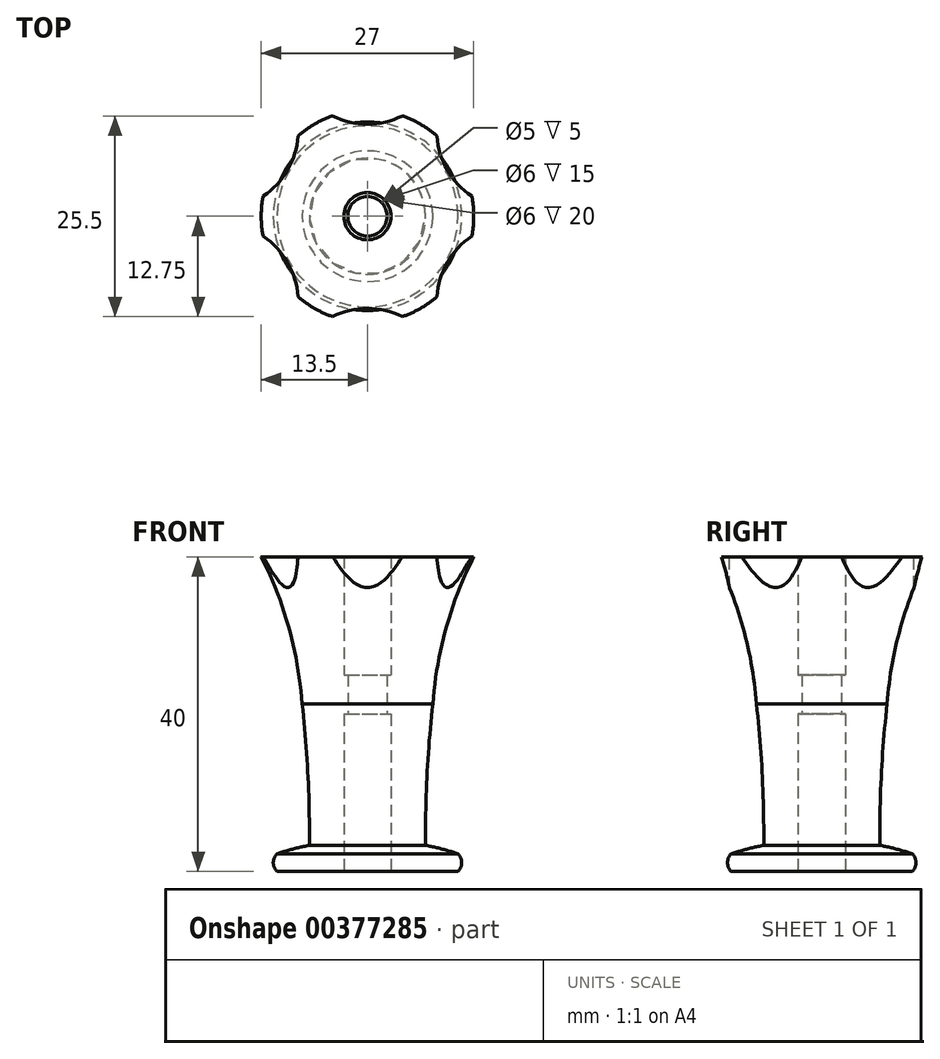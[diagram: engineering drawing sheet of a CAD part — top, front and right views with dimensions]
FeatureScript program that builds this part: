
annotation { "Feature Type Name" : "Feature", "Feature Type Description" : "" }
export const myFeature = defineFeature(function(context is Context, id is Id, definition is map)
    precondition{}
    {
        {
            var Q0;
            Q0=qCreatedBy(makeId("Front.planeOp"),FACE);
            var sketch = newSketch(context, id + "F0", { "sketchPlane" : qUnion([Q0])});
            skLineSegment(sketch, "E0", {"start": v(0, 19.97) * mm, "end": v(0, -20.03) * mm});
            skLineSegment(sketch, "E1", {"start": v(0, 19.97) * mm, "end": v(13.5, 19.97) * mm});
            skLineSegment(sketch, "E2", {"start": v(0, -20.03) * mm, "end": v(11.5, -20.03) * mm});
            skArc(sketch, "E3", {"start": v(11.5, -20.03) * mm, "mid": v(11.97, -18.9) * mm, "end": v(11.5, -17.77) * mm});
            skArc(sketch, "E4", {"start": v(11.5, -17.77) * mm, "mid": v(9.46, -17.16) * mm, "end": v(7.37, -16.69) * mm});
            skArc(sketch, "E5", {"start": v(13.5, 19.97) * mm, "mid": v(9.97, 10.87) * mm, "end": v(8.3, 1.26) * mm});
            skArc(sketch, "E6", {"start": v(8.3, 1.26) * mm, "mid": v(7.57, -7.7) * mm, "end": v(7.37, -16.69) * mm});
            skSolve(sketch);
        }
        {
            var Q0;
            Q0 = qSketchRegion(id + "F0", true);
            var Q1;
            Q1=sQuery(id+"F0.wireOp",EDGE,"E0");
            revolve(context, id + "F1", {"entities" : qUnion([Q0]), "axis" : qUnion([Q1]), "revolveType" : RevolveType.FULL});
        }
        {
            var Q0;
            Q0=makeQuery(id+"F1.opRevolve","SWEPT_FACE",FACE,{"disambiguationData":[OSD([sQuery(id+"F0.wireOp",EDGE,"E1")])]});
            var sketch = newSketch(context, id + "F2", { "sketchPlane" : qUnion([Q0])});
            skCircle(sketch, "E7.cCircle", {"center": v(0, 0) * mm, "radius": 13.5 * mm, "construction": true});
            skLineSegment(sketch, "E7.0", {"start": v(-13.5, -7.8) * mm, "end": v(-13.5, 7.8) * mm});
            skLineSegment(sketch, "E7.1", {"start": v(-13.5, 7.8) * mm, "end": v(0, 15.59) * mm});
            skLineSegment(sketch, "E7.2", {"start": v(0, 15.59) * mm, "end": v(13.5, 7.8) * mm});
            skLineSegment(sketch, "E7.3", {"start": v(13.5, 7.8) * mm, "end": v(13.5, -7.8) * mm});
            skLineSegment(sketch, "E7.4", {"start": v(13.5, -7.8) * mm, "end": v(0, -15.59) * mm});
            skLineSegment(sketch, "E7.5", {"start": v(0, -15.59) * mm, "end": v(-13.5, -7.8) * mm});
            skPoint(sketch, "E7.0.midPoint", {"position": v(-13.5, 0) * mm});
            skLineSegment(sketch, "E8.0", {"start": v(-13.5, -4.91) * mm, "end": v(-13.5, 4.91) * mm});
            skLineSegment(sketch, "E8.1", {"start": v(-13.5, 4.91) * mm, "end": v(-7.18, 12.44) * mm});
            skLineSegment(sketch, "E8.2", {"start": v(-7.18, 12.44) * mm, "end": v(2.5, 14.15) * mm});
            skLineSegment(sketch, "E8.3", {"start": v(2.5, 14.15) * mm, "end": v(11, 9.23) * mm});
            skLineSegment(sketch, "E8.4", {"start": v(11, 9.23) * mm, "end": v(14.37, 0) * mm});
            skLineSegment(sketch, "E8.5", {"start": v(14.37, 0) * mm, "end": v(11, -9.23) * mm});
            skLineSegment(sketch, "E8.6", {"start": v(11, -9.23) * mm, "end": v(2.5, -14.15) * mm});
            skLineSegment(sketch, "E8.7", {"start": v(2.5, -14.15) * mm, "end": v(-7.18, -12.44) * mm});
            skLineSegment(sketch, "E8.8", {"start": v(-7.18, -12.44) * mm, "end": v(-13.5, -4.91) * mm});
            skLineSegment(sketch, "E9.0", {"start": v(13.5, 4.91) * mm, "end": v(13.5, -4.91) * mm});
            skLineSegment(sketch, "E9.1", {"start": v(13.5, -4.91) * mm, "end": v(7.18, -12.44) * mm});
            skLineSegment(sketch, "E9.2", {"start": v(7.18, -12.44) * mm, "end": v(-2.5, -14.15) * mm});
            skLineSegment(sketch, "E9.3", {"start": v(-2.5, -14.15) * mm, "end": v(-11, -9.23) * mm});
            skLineSegment(sketch, "E9.4", {"start": v(-11, -9.23) * mm, "end": v(-14.37, 0) * mm});
            skLineSegment(sketch, "E9.5", {"start": v(-14.37, 0) * mm, "end": v(-11, 9.23) * mm});
            skLineSegment(sketch, "E9.6", {"start": v(-11, 9.23) * mm, "end": v(-2.5, 14.15) * mm});
            skLineSegment(sketch, "E9.7", {"start": v(-2.5, 14.15) * mm, "end": v(7.18, 12.44) * mm});
            skLineSegment(sketch, "E9.8", {"start": v(7.18, 12.44) * mm, "end": v(13.5, 4.91) * mm});
            skPoint(sketch, "E9.0.midPoint", {"position": v(13.5, 0) * mm});
            skArc(sketch, "E10", {"start": v(-4.69, 12.88) * mm, "mid": v(0, 11.71) * mm, "end": v(4.69, 12.88) * mm});
            skArc(sketch, "E11", {"start": v(4.69, -12.88) * mm, "mid": v(0, -11.71) * mm, "end": v(-4.69, -12.88) * mm});
            skArc(sketch, "E12", {"start": v(-13.5, 2.38) * mm, "mid": v(-10.14, 5.86) * mm, "end": v(-8.81, 10.5) * mm});
            skArc(sketch, "E13", {"start": v(-8.81, -10.5) * mm, "mid": v(-10.14, -5.86) * mm, "end": v(-13.5, -2.38) * mm});
            skArc(sketch, "E14", {"start": v(13.5, -2.38) * mm, "mid": v(10.14, -5.86) * mm, "end": v(8.81, -10.5) * mm});
            skArc(sketch, "E15", {"start": v(8.81, 10.5) * mm, "mid": v(10.14, 5.86) * mm, "end": v(13.5, 2.38) * mm});
            skCircle(sketch, "E16", {"center": v(0, 0) * mm, "radius": 11.23 * mm});
            skSolve(sketch);
        }
        {
            var Q0;
            Q0=makeQuery(id+"F1.opRevolve","SWEPT_FACE",FACE,{"disambiguationData":[OSD([sQuery(id+"F0.wireOp",EDGE,"E2")])]});
            var sketch = newSketch(context, id + "F3", { "sketchPlane" : qUnion([Q0])});
            skCircle(sketch, "E17", {"center": v(0, 0) * mm, "radius": 3 * mm});
            skSolve(sketch);
        }
        {
            var Q0;
            Q0 = qSketchRegion(id + "F3", true);
            extrude(context, id + "F4", {"entities" : qUnion([Q0]), "operationType" : NewBodyOperationType.REMOVE, "oppositeDirection" : true, "depth" : 50 * mm});
        }
        {
            var Q0;
            {var subQ0=sQuery(id+"F2.wireOp",EDGE,"E7.5");var subQ1=sQuery(id+"F2.wireOp",EDGE,"E7.0");var subQ2=makeQuery(id+"F2.imprint","INTERSECT",VERTEX,{"derivedFrom":[subQ1,subQ0]});Q0=makeQuery(id+"F2.imprint","IMPRINT",FACE,{"disambiguationData":[TD([[makeQuery(id+"F2.imprint","IMPRINT",EDGE,{"disambiguationData":[TD([[subQ2,-1.0]])],"derivedFrom":subQ1}),-1.0]])]});}
            var Q1;
            {var subQ0=sQuery(id+"F2.wireOp",EDGE,"E7.1");var subQ1=sQuery(id+"F2.wireOp",EDGE,"E7.0");var subQ2=makeQuery(id+"F2.imprint","INTERSECT",VERTEX,{"derivedFrom":[subQ1,subQ0]});Q1=makeQuery(id+"F2.imprint","IMPRINT",FACE,{"disambiguationData":[TD([[makeQuery(id+"F2.imprint","IMPRINT",EDGE,{"disambiguationData":[TD([[subQ2,1.0]])],"derivedFrom":subQ1}),-1.0]])]});}
            var Q2;
            {var subQ0=sQuery(id+"F2.wireOp",EDGE,"E7.2");var subQ1=sQuery(id+"F2.wireOp",EDGE,"E7.1");var subQ2=makeQuery(id+"F2.imprint","INTERSECT",VERTEX,{"derivedFrom":[subQ1,subQ0]});Q2=makeQuery(id+"F2.imprint","IMPRINT",FACE,{"disambiguationData":[TD([[makeQuery(id+"F2.imprint","IMPRINT",EDGE,{"disambiguationData":[TD([[subQ2,1.0]])],"derivedFrom":subQ1}),-1.0]])]});}
            var Q3;
            {var subQ0=sQuery(id+"F2.wireOp",EDGE,"E7.3");var subQ1=sQuery(id+"F2.wireOp",EDGE,"E7.2");var subQ2=makeQuery(id+"F2.imprint","INTERSECT",VERTEX,{"derivedFrom":[subQ1,subQ0]});Q3=makeQuery(id+"F2.imprint","IMPRINT",FACE,{"disambiguationData":[TD([[makeQuery(id+"F2.imprint","IMPRINT",EDGE,{"disambiguationData":[TD([[subQ2,1.0]])],"derivedFrom":subQ1}),-1.0]])]});}
            var Q4;
            {var subQ0=sQuery(id+"F2.wireOp",EDGE,"E7.4");var subQ1=sQuery(id+"F2.wireOp",EDGE,"E7.3");var subQ2=makeQuery(id+"F2.imprint","INTERSECT",VERTEX,{"derivedFrom":[subQ1,subQ0]});Q4=makeQuery(id+"F2.imprint","IMPRINT",FACE,{"disambiguationData":[TD([[makeQuery(id+"F2.imprint","IMPRINT",EDGE,{"disambiguationData":[TD([[subQ2,1.0]])],"derivedFrom":subQ1}),-1.0]])]});}
            var Q5;
            {var subQ0=sQuery(id+"F2.wireOp",EDGE,"E7.5");var subQ1=sQuery(id+"F2.wireOp",EDGE,"E7.4");var subQ2=makeQuery(id+"F2.imprint","INTERSECT",VERTEX,{"derivedFrom":[subQ1,subQ0]});Q5=makeQuery(id+"F2.imprint","IMPRINT",FACE,{"disambiguationData":[TD([[makeQuery(id+"F2.imprint","IMPRINT",EDGE,{"disambiguationData":[TD([[subQ2,1.0]])],"derivedFrom":subQ1}),-1.0]])]});}
            var Q6;
            {var subQ0=sQuery(id+"F2.wireOp",EDGE,"E9.4");var subQ4=sQuery(id+"F2.wireOp",EDGE,"E9.5");var subQ5=makeQuery(id+"F2.imprint","INTERSECT",VERTEX,{"derivedFrom":[subQ0,subQ4]});Q6=makeQuery(id+"F2.imprint","IMPRINT",FACE,{"disambiguationData":[TD([[makeQuery(id+"F2.imprint","IMPRINT",EDGE,{"disambiguationData":[TD([[subQ5,1.0]])],"derivedFrom":subQ0}),-1.0]])]});}
            var Q7;
            {var subQ0=sQuery(id+"F2.wireOp",EDGE,"E8.2");var subQ1=sQuery(id+"F2.wireOp",EDGE,"E8.1");var subQ2=makeQuery(id+"F2.imprint","INTERSECT",VERTEX,{"derivedFrom":[subQ1,subQ0]});Q7=makeQuery(id+"F2.imprint","IMPRINT",FACE,{"disambiguationData":[TD([[makeQuery(id+"F2.imprint","IMPRINT",EDGE,{"disambiguationData":[TD([[subQ2,1.0]])],"derivedFrom":subQ1}),-1.0]])]});}
            var Q8;
            {var subQ0=sQuery(id+"F2.wireOp",EDGE,"E9.7");var subQ4=sQuery(id+"F2.wireOp",EDGE,"E9.8");var subQ5=makeQuery(id+"F2.imprint","INTERSECT",VERTEX,{"derivedFrom":[subQ0,subQ4]});Q8=makeQuery(id+"F2.imprint","IMPRINT",FACE,{"disambiguationData":[TD([[makeQuery(id+"F2.imprint","IMPRINT",EDGE,{"disambiguationData":[TD([[subQ5,1.0]])],"derivedFrom":subQ0}),-1.0]])]});}
            var Q9;
            {var subQ0=sQuery(id+"F2.wireOp",EDGE,"E8.5");var subQ1=sQuery(id+"F2.wireOp",EDGE,"E8.4");var subQ2=makeQuery(id+"F2.imprint","INTERSECT",VERTEX,{"derivedFrom":[subQ1,subQ0]});Q9=makeQuery(id+"F2.imprint","IMPRINT",FACE,{"disambiguationData":[TD([[makeQuery(id+"F2.imprint","IMPRINT",EDGE,{"disambiguationData":[TD([[subQ2,1.0]])],"derivedFrom":subQ1}),-1.0]])]});}
            var Q10;
            {var subQ0=sQuery(id+"F2.wireOp",EDGE,"E9.1");var subQ4=sQuery(id+"F2.wireOp",EDGE,"E9.2");var subQ6=makeQuery(id+"F2.imprint","INTERSECT",VERTEX,{"derivedFrom":[subQ0,subQ4]});Q10=makeQuery(id+"F2.imprint","IMPRINT",FACE,{"disambiguationData":[TD([[makeQuery(id+"F2.imprint","IMPRINT",EDGE,{"disambiguationData":[TD([[subQ6,1.0]])],"derivedFrom":subQ0}),-1.0]])]});}
            var Q11;
            {var subQ0=sQuery(id+"F2.wireOp",EDGE,"E8.8");var subQ1=sQuery(id+"F2.wireOp",EDGE,"E8.7");var subQ2=makeQuery(id+"F2.imprint","INTERSECT",VERTEX,{"derivedFrom":[subQ1,subQ0]});Q11=makeQuery(id+"F2.imprint","IMPRINT",FACE,{"disambiguationData":[TD([[makeQuery(id+"F2.imprint","IMPRINT",EDGE,{"disambiguationData":[TD([[subQ2,1.0]])],"derivedFrom":subQ1}),-1.0]])]});}
            var Q12;
            {var subQ0=sQuery(id+"F2.wireOp",EDGE,"E8.8");var subQ3=sQuery(id+"F2.wireOp",EDGE,"E9.4");var subQ5=makeQuery(id+"F2.imprint","INTERSECT",VERTEX,{"derivedFrom":[subQ0,subQ3]});Q12=makeQuery(id+"F2.imprint","IMPRINT",FACE,{"disambiguationData":[TD([[makeQuery(id+"F2.imprint","IMPRINT",EDGE,{"disambiguationData":[TD([[subQ5,-1.0]])],"derivedFrom":subQ0}),-1.0]])]});}
            var Q13;
            {var subQ0=sQuery(id+"F2.wireOp",EDGE,"E8.1");var subQ3=sQuery(id+"F2.wireOp",EDGE,"E9.5");var subQ5=makeQuery(id+"F2.imprint","INTERSECT",VERTEX,{"derivedFrom":[subQ0,subQ3]});Q13=makeQuery(id+"F2.imprint","IMPRINT",FACE,{"disambiguationData":[TD([[makeQuery(id+"F2.imprint","IMPRINT",EDGE,{"disambiguationData":[TD([[subQ5,1.0]])],"derivedFrom":subQ0}),-1.0]])]});}
            var Q14;
            {var subQ0=sQuery(id+"F2.wireOp",EDGE,"E9.5");var subQ1=sQuery(id+"F2.wireOp",EDGE,"E8.1");var subQ2=makeQuery(id+"F2.imprint","INTERSECT",VERTEX,{"derivedFrom":[subQ1,subQ0]});Q14=makeQuery(id+"F2.imprint","IMPRINT",FACE,{"disambiguationData":[TD([[makeQuery(id+"F2.imprint","IMPRINT",EDGE,{"disambiguationData":[TD([[subQ2,-1.0]])],"derivedFrom":subQ1}),1.0]])]});}
            var Q15;
            {var subQ1=sQuery(id+"F2.wireOp",EDGE,"E8.2");var subQ4=sQuery(id+"F2.wireOp",EDGE,"E9.7");var subQ6=makeQuery(id+"F2.imprint","INTERSECT",VERTEX,{"derivedFrom":[subQ1,subQ4]});Q15=makeQuery(id+"F2.imprint","IMPRINT",FACE,{"disambiguationData":[TD([[makeQuery(id+"F2.imprint","IMPRINT",EDGE,{"disambiguationData":[TD([[subQ6,1.0]])],"derivedFrom":subQ1}),1.0]])]});}
            var Q16;
            {var subQ1=sQuery(id+"F2.wireOp",EDGE,"E8.2");var subQ3=sQuery(id+"F2.wireOp",EDGE,"E9.7");var subQ4=makeQuery(id+"F2.imprint","INTERSECT",VERTEX,{"derivedFrom":[subQ1,subQ3]});Q16=makeQuery(id+"F2.imprint","IMPRINT",FACE,{"disambiguationData":[TD([[makeQuery(id+"F2.imprint","IMPRINT",EDGE,{"disambiguationData":[TD([[subQ4,-1.0]])],"derivedFrom":subQ1}),-1.0]])]});}
            var Q17;
            {var subQ0=sQuery(id+"F2.wireOp",EDGE,"E8.4");var subQ3=sQuery(id+"F2.wireOp",EDGE,"E9.8");var subQ5=makeQuery(id+"F2.imprint","INTERSECT",VERTEX,{"derivedFrom":[subQ0,subQ3]});Q17=makeQuery(id+"F2.imprint","IMPRINT",FACE,{"disambiguationData":[TD([[makeQuery(id+"F2.imprint","IMPRINT",EDGE,{"disambiguationData":[TD([[subQ5,1.0]])],"derivedFrom":subQ0}),-1.0]])]});}
            var Q18;
            {var subQ0=sQuery(id+"F2.wireOp",EDGE,"E9.8");var subQ1=sQuery(id+"F2.wireOp",EDGE,"E8.4");var subQ2=makeQuery(id+"F2.imprint","INTERSECT",VERTEX,{"derivedFrom":[subQ1,subQ0]});Q18=makeQuery(id+"F2.imprint","IMPRINT",FACE,{"disambiguationData":[TD([[makeQuery(id+"F2.imprint","IMPRINT",EDGE,{"disambiguationData":[TD([[subQ2,-1.0]])],"derivedFrom":subQ1}),1.0]])]});}
            var Q19;
            {var subQ1=sQuery(id+"F2.wireOp",EDGE,"E8.5");var subQ4=sQuery(id+"F2.wireOp",EDGE,"E9.1");var subQ5=makeQuery(id+"F2.imprint","INTERSECT",VERTEX,{"derivedFrom":[subQ1,subQ4]});Q19=makeQuery(id+"F2.imprint","IMPRINT",FACE,{"disambiguationData":[TD([[makeQuery(id+"F2.imprint","IMPRINT",EDGE,{"disambiguationData":[TD([[subQ5,1.0]])],"derivedFrom":subQ1}),1.0]])]});}
            var Q20;
            {var subQ1=sQuery(id+"F2.wireOp",EDGE,"E8.5");var subQ3=sQuery(id+"F2.wireOp",EDGE,"E9.1");var subQ4=makeQuery(id+"F2.imprint","INTERSECT",VERTEX,{"derivedFrom":[subQ1,subQ3]});Q20=makeQuery(id+"F2.imprint","IMPRINT",FACE,{"disambiguationData":[TD([[makeQuery(id+"F2.imprint","IMPRINT",EDGE,{"disambiguationData":[TD([[subQ4,-1.0]])],"derivedFrom":subQ1}),-1.0]])]});}
            var Q21;
            {var subQ0=sQuery(id+"F2.wireOp",EDGE,"E8.7");var subQ3=sQuery(id+"F2.wireOp",EDGE,"E9.2");var subQ5=makeQuery(id+"F2.imprint","INTERSECT",VERTEX,{"derivedFrom":[subQ0,subQ3]});Q21=makeQuery(id+"F2.imprint","IMPRINT",FACE,{"disambiguationData":[TD([[makeQuery(id+"F2.imprint","IMPRINT",EDGE,{"disambiguationData":[TD([[subQ5,1.0]])],"derivedFrom":subQ0}),-1.0]])]});}
            var Q22;
            {var subQ0=sQuery(id+"F2.wireOp",EDGE,"E9.2");var subQ1=sQuery(id+"F2.wireOp",EDGE,"E8.7");var subQ2=makeQuery(id+"F2.imprint","INTERSECT",VERTEX,{"derivedFrom":[subQ1,subQ0]});Q22=makeQuery(id+"F2.imprint","IMPRINT",FACE,{"disambiguationData":[TD([[makeQuery(id+"F2.imprint","IMPRINT",EDGE,{"disambiguationData":[TD([[subQ2,-1.0]])],"derivedFrom":subQ1}),1.0]])]});}
            var Q23;
            {var subQ1=sQuery(id+"F2.wireOp",EDGE,"E8.8");var subQ4=sQuery(id+"F2.wireOp",EDGE,"E9.4");var subQ5=makeQuery(id+"F2.imprint","INTERSECT",VERTEX,{"derivedFrom":[subQ1,subQ4]});Q23=makeQuery(id+"F2.imprint","IMPRINT",FACE,{"disambiguationData":[TD([[makeQuery(id+"F2.imprint","IMPRINT",EDGE,{"disambiguationData":[TD([[subQ5,1.0]])],"derivedFrom":subQ1}),1.0]])]});}
            var Q24;
            {var subQ0=sQuery(id+"F2.wireOp",EDGE,"E13");var subQ1=sQuery(id+"F2.wireOp",EDGE,"E8.0");var subQ2=makeQuery(id+"F2.imprint","INTERSECT",VERTEX,{"derivedFrom":[subQ1,sQuery(id+"F2.wireOp",EDGE,"E9.4"),subQ0]});Q24=makeQuery(id+"F2.imprint","IMPRINT",FACE,{"disambiguationData":[TD([[makeQuery(id+"F2.imprint","IMPRINT",EDGE,{"disambiguationData":[TD([[subQ2,-1.0]])],"derivedFrom":subQ1}),-1.0]])]});}
            var Q25;
            {var subQ0=sQuery(id+"F2.wireOp",EDGE,"E12");var subQ1=sQuery(id+"F2.wireOp",EDGE,"E8.0");var subQ2=makeQuery(id+"F2.imprint","INTERSECT",VERTEX,{"derivedFrom":[subQ1,sQuery(id+"F2.wireOp",EDGE,"E9.5"),subQ0]});Q25=makeQuery(id+"F2.imprint","IMPRINT",FACE,{"disambiguationData":[TD([[makeQuery(id+"F2.imprint","IMPRINT",EDGE,{"disambiguationData":[TD([[subQ2,1.0]])],"derivedFrom":subQ1}),-1.0]])]});}
            var Q26;
            {var subQ0=sQuery(id+"F2.wireOp",EDGE,"E9.5");var subQ1=sQuery(id+"F2.wireOp",EDGE,"E8.1");var subQ2=makeQuery(id+"F2.imprint","INTERSECT",VERTEX,{"derivedFrom":[subQ1,subQ0]});Q26=makeQuery(id+"F2.imprint","IMPRINT",FACE,{"disambiguationData":[TD([[makeQuery(id+"F2.imprint","IMPRINT",EDGE,{"disambiguationData":[TD([[subQ2,-1.0]])],"derivedFrom":subQ1}),-1.0]])]});}
            var Q27;
            {var subQ0=sQuery(id+"F2.wireOp",EDGE,"E12");var subQ1=sQuery(id+"F2.wireOp",EDGE,"E8.1");var subQ2=makeQuery(id+"F2.imprint","INTERSECT",VERTEX,{"derivedFrom":[subQ1,sQuery(id+"F2.wireOp",EDGE,"E9.6"),subQ0]});Q27=makeQuery(id+"F2.imprint","IMPRINT",FACE,{"disambiguationData":[TD([[makeQuery(id+"F2.imprint","IMPRINT",EDGE,{"disambiguationData":[TD([[subQ2,1.0]])],"derivedFrom":subQ1}),-1.0]])]});}
            var Q28;
            {var subQ0=sQuery(id+"F2.wireOp",EDGE,"E10");var subQ1=sQuery(id+"F2.wireOp",EDGE,"E8.2");var subQ2=makeQuery(id+"F2.imprint","INTERSECT",VERTEX,{"derivedFrom":[subQ1,sQuery(id+"F2.wireOp",EDGE,"E9.6"),subQ0]});Q28=makeQuery(id+"F2.imprint","IMPRINT",FACE,{"disambiguationData":[TD([[makeQuery(id+"F2.imprint","IMPRINT",EDGE,{"disambiguationData":[TD([[subQ2,-1.0]])],"derivedFrom":subQ1}),-1.0]])]});}
            var Q29;
            {var subQ0=sQuery(id+"F2.wireOp",EDGE,"E9.7");var subQ1=sQuery(id+"F2.wireOp",EDGE,"E8.2");var subQ2=makeQuery(id+"F2.imprint","INTERSECT",VERTEX,{"derivedFrom":[subQ1,subQ0]});Q29=makeQuery(id+"F2.imprint","IMPRINT",FACE,{"disambiguationData":[TD([[makeQuery(id+"F2.imprint","IMPRINT",EDGE,{"disambiguationData":[TD([[subQ2,1.0]])],"derivedFrom":subQ1}),-1.0]])]});}
            var Q30;
            {var subQ0=sQuery(id+"F2.wireOp",EDGE,"E10");var subQ1=sQuery(id+"F2.wireOp",EDGE,"E8.3");var subQ2=makeQuery(id+"F2.imprint","INTERSECT",VERTEX,{"derivedFrom":[subQ1,sQuery(id+"F2.wireOp",EDGE,"E9.7"),subQ0]});Q30=makeQuery(id+"F2.imprint","IMPRINT",FACE,{"disambiguationData":[TD([[makeQuery(id+"F2.imprint","IMPRINT",EDGE,{"disambiguationData":[TD([[subQ2,-1.0]])],"derivedFrom":subQ1}),-1.0]])]});}
            var Q31;
            {var subQ0=sQuery(id+"F2.wireOp",EDGE,"E15");var subQ1=sQuery(id+"F2.wireOp",EDGE,"E8.3");var subQ2=makeQuery(id+"F2.imprint","INTERSECT",VERTEX,{"derivedFrom":[subQ1,sQuery(id+"F2.wireOp",EDGE,"E9.8"),subQ0]});Q31=makeQuery(id+"F2.imprint","IMPRINT",FACE,{"disambiguationData":[TD([[makeQuery(id+"F2.imprint","IMPRINT",EDGE,{"disambiguationData":[TD([[subQ2,1.0]])],"derivedFrom":subQ1}),-1.0]])]});}
            var Q32;
            {var subQ0=sQuery(id+"F2.wireOp",EDGE,"E9.8");var subQ1=sQuery(id+"F2.wireOp",EDGE,"E8.4");var subQ2=makeQuery(id+"F2.imprint","INTERSECT",VERTEX,{"derivedFrom":[subQ1,subQ0]});Q32=makeQuery(id+"F2.imprint","IMPRINT",FACE,{"disambiguationData":[TD([[makeQuery(id+"F2.imprint","IMPRINT",EDGE,{"disambiguationData":[TD([[subQ2,-1.0]])],"derivedFrom":subQ1}),-1.0]])]});}
            var Q33;
            {var subQ0=sQuery(id+"F2.wireOp",EDGE,"E15");var subQ1=sQuery(id+"F2.wireOp",EDGE,"E8.4");var subQ2=makeQuery(id+"F2.imprint","INTERSECT",VERTEX,{"derivedFrom":[subQ1,sQuery(id+"F2.wireOp",EDGE,"E9.0"),subQ0]});Q33=makeQuery(id+"F2.imprint","IMPRINT",FACE,{"disambiguationData":[TD([[makeQuery(id+"F2.imprint","IMPRINT",EDGE,{"disambiguationData":[TD([[subQ2,1.0]])],"derivedFrom":subQ1}),-1.0]])]});}
            var Q34;
            {var subQ0=sQuery(id+"F2.wireOp",EDGE,"E14");var subQ1=sQuery(id+"F2.wireOp",EDGE,"E8.5");var subQ2=makeQuery(id+"F2.imprint","INTERSECT",VERTEX,{"derivedFrom":[subQ1,sQuery(id+"F2.wireOp",EDGE,"E9.0"),subQ0]});Q34=makeQuery(id+"F2.imprint","IMPRINT",FACE,{"disambiguationData":[TD([[makeQuery(id+"F2.imprint","IMPRINT",EDGE,{"disambiguationData":[TD([[subQ2,-1.0]])],"derivedFrom":subQ1}),-1.0]])]});}
            var Q35;
            {var subQ0=sQuery(id+"F2.wireOp",EDGE,"E9.1");var subQ1=sQuery(id+"F2.wireOp",EDGE,"E8.5");var subQ2=makeQuery(id+"F2.imprint","INTERSECT",VERTEX,{"derivedFrom":[subQ1,subQ0]});Q35=makeQuery(id+"F2.imprint","IMPRINT",FACE,{"disambiguationData":[TD([[makeQuery(id+"F2.imprint","IMPRINT",EDGE,{"disambiguationData":[TD([[subQ2,1.0]])],"derivedFrom":subQ1}),-1.0]])]});}
            var Q36;
            {var subQ0=sQuery(id+"F2.wireOp",EDGE,"E14");var subQ1=sQuery(id+"F2.wireOp",EDGE,"E8.6");var subQ2=makeQuery(id+"F2.imprint","INTERSECT",VERTEX,{"derivedFrom":[subQ1,sQuery(id+"F2.wireOp",EDGE,"E9.1"),subQ0]});Q36=makeQuery(id+"F2.imprint","IMPRINT",FACE,{"disambiguationData":[TD([[makeQuery(id+"F2.imprint","IMPRINT",EDGE,{"disambiguationData":[TD([[subQ2,-1.0]])],"derivedFrom":subQ1}),-1.0]])]});}
            var Q37;
            {var subQ0=sQuery(id+"F2.wireOp",EDGE,"E11");var subQ1=sQuery(id+"F2.wireOp",EDGE,"E8.6");var subQ2=makeQuery(id+"F2.imprint","INTERSECT",VERTEX,{"derivedFrom":[subQ1,sQuery(id+"F2.wireOp",EDGE,"E9.2"),subQ0]});Q37=makeQuery(id+"F2.imprint","IMPRINT",FACE,{"disambiguationData":[TD([[makeQuery(id+"F2.imprint","IMPRINT",EDGE,{"disambiguationData":[TD([[subQ2,1.0]])],"derivedFrom":subQ1}),-1.0]])]});}
            var Q38;
            {var subQ0=sQuery(id+"F2.wireOp",EDGE,"E9.2");var subQ1=sQuery(id+"F2.wireOp",EDGE,"E8.7");var subQ2=makeQuery(id+"F2.imprint","INTERSECT",VERTEX,{"derivedFrom":[subQ1,subQ0]});Q38=makeQuery(id+"F2.imprint","IMPRINT",FACE,{"disambiguationData":[TD([[makeQuery(id+"F2.imprint","IMPRINT",EDGE,{"disambiguationData":[TD([[subQ2,-1.0]])],"derivedFrom":subQ1}),-1.0]])]});}
            var Q39;
            {var subQ0=sQuery(id+"F2.wireOp",EDGE,"E11");var subQ1=sQuery(id+"F2.wireOp",EDGE,"E8.7");var subQ2=makeQuery(id+"F2.imprint","INTERSECT",VERTEX,{"derivedFrom":[subQ1,sQuery(id+"F2.wireOp",EDGE,"E9.3"),subQ0]});Q39=makeQuery(id+"F2.imprint","IMPRINT",FACE,{"disambiguationData":[TD([[makeQuery(id+"F2.imprint","IMPRINT",EDGE,{"disambiguationData":[TD([[subQ2,1.0]])],"derivedFrom":subQ1}),-1.0]])]});}
            var Q40;
            {var subQ0=sQuery(id+"F2.wireOp",EDGE,"E13");var subQ1=sQuery(id+"F2.wireOp",EDGE,"E8.8");var subQ2=makeQuery(id+"F2.imprint","INTERSECT",VERTEX,{"derivedFrom":[subQ1,sQuery(id+"F2.wireOp",EDGE,"E9.3"),subQ0]});Q40=makeQuery(id+"F2.imprint","IMPRINT",FACE,{"disambiguationData":[TD([[makeQuery(id+"F2.imprint","IMPRINT",EDGE,{"disambiguationData":[TD([[subQ2,-1.0]])],"derivedFrom":subQ1}),-1.0]])]});}
            var Q41;
            {var subQ0=sQuery(id+"F2.wireOp",EDGE,"E9.4");var subQ1=sQuery(id+"F2.wireOp",EDGE,"E8.8");var subQ2=makeQuery(id+"F2.imprint","INTERSECT",VERTEX,{"derivedFrom":[subQ1,subQ0]});Q41=makeQuery(id+"F2.imprint","IMPRINT",FACE,{"disambiguationData":[TD([[makeQuery(id+"F2.imprint","IMPRINT",EDGE,{"disambiguationData":[TD([[subQ2,1.0]])],"derivedFrom":subQ1}),-1.0]])]});}
            var Q42;
            {var subQ0=sQuery(id+"F2.wireOp",EDGE,"E15");var subQ1=sQuery(id+"F2.wireOp",EDGE,"E9.0");var subQ2=makeQuery(id+"F2.imprint","INTERSECT",VERTEX,{"derivedFrom":[sQuery(id+"F2.wireOp",EDGE,"E8.4"),subQ1,subQ0]});Q42=makeQuery(id+"F2.imprint","IMPRINT",FACE,{"disambiguationData":[TD([[makeQuery(id+"F2.imprint","IMPRINT",EDGE,{"disambiguationData":[TD([[subQ2,-1.0]])],"derivedFrom":subQ1}),-1.0]])]});}
            var Q43;
            {var subQ0=sQuery(id+"F2.wireOp",EDGE,"E14");var subQ1=sQuery(id+"F2.wireOp",EDGE,"E9.0");var subQ2=makeQuery(id+"F2.imprint","INTERSECT",VERTEX,{"derivedFrom":[sQuery(id+"F2.wireOp",EDGE,"E8.5"),subQ1,subQ0]});Q43=makeQuery(id+"F2.imprint","IMPRINT",FACE,{"disambiguationData":[TD([[makeQuery(id+"F2.imprint","IMPRINT",EDGE,{"disambiguationData":[TD([[subQ2,1.0]])],"derivedFrom":subQ1}),-1.0]])]});}
            var Q44;
            {var subQ0=sQuery(id+"F2.wireOp",EDGE,"E14");var subQ1=sQuery(id+"F2.wireOp",EDGE,"E9.1");var subQ2=makeQuery(id+"F2.imprint","INTERSECT",VERTEX,{"derivedFrom":[sQuery(id+"F2.wireOp",EDGE,"E8.6"),subQ1,subQ0]});Q44=makeQuery(id+"F2.imprint","IMPRINT",FACE,{"disambiguationData":[TD([[makeQuery(id+"F2.imprint","IMPRINT",EDGE,{"disambiguationData":[TD([[subQ2,1.0]])],"derivedFrom":subQ1}),-1.0]])]});}
            var Q45;
            {var subQ0=sQuery(id+"F2.wireOp",EDGE,"E11");var subQ1=sQuery(id+"F2.wireOp",EDGE,"E9.2");var subQ2=makeQuery(id+"F2.imprint","INTERSECT",VERTEX,{"derivedFrom":[sQuery(id+"F2.wireOp",EDGE,"E8.6"),subQ1,subQ0]});Q45=makeQuery(id+"F2.imprint","IMPRINT",FACE,{"disambiguationData":[TD([[makeQuery(id+"F2.imprint","IMPRINT",EDGE,{"disambiguationData":[TD([[subQ2,-1.0]])],"derivedFrom":subQ1}),-1.0]])]});}
            var Q46;
            {var subQ0=sQuery(id+"F2.wireOp",EDGE,"E11");var subQ1=sQuery(id+"F2.wireOp",EDGE,"E9.3");var subQ2=makeQuery(id+"F2.imprint","INTERSECT",VERTEX,{"derivedFrom":[sQuery(id+"F2.wireOp",EDGE,"E8.7"),subQ1,subQ0]});Q46=makeQuery(id+"F2.imprint","IMPRINT",FACE,{"disambiguationData":[TD([[makeQuery(id+"F2.imprint","IMPRINT",EDGE,{"disambiguationData":[TD([[subQ2,-1.0]])],"derivedFrom":subQ1}),-1.0]])]});}
            var Q47;
            {var subQ0=sQuery(id+"F2.wireOp",EDGE,"E13");var subQ1=sQuery(id+"F2.wireOp",EDGE,"E9.3");var subQ2=makeQuery(id+"F2.imprint","INTERSECT",VERTEX,{"derivedFrom":[sQuery(id+"F2.wireOp",EDGE,"E8.8"),subQ1,subQ0]});Q47=makeQuery(id+"F2.imprint","IMPRINT",FACE,{"disambiguationData":[TD([[makeQuery(id+"F2.imprint","IMPRINT",EDGE,{"disambiguationData":[TD([[subQ2,1.0]])],"derivedFrom":subQ1}),-1.0]])]});}
            var Q48;
            {var subQ0=sQuery(id+"F2.wireOp",EDGE,"E13");var subQ1=sQuery(id+"F2.wireOp",EDGE,"E9.4");var subQ2=makeQuery(id+"F2.imprint","INTERSECT",VERTEX,{"derivedFrom":[sQuery(id+"F2.wireOp",EDGE,"E8.0"),subQ1,subQ0]});Q48=makeQuery(id+"F2.imprint","IMPRINT",FACE,{"disambiguationData":[TD([[makeQuery(id+"F2.imprint","IMPRINT",EDGE,{"disambiguationData":[TD([[subQ2,1.0]])],"derivedFrom":subQ1}),-1.0]])]});}
            var Q49;
            {var subQ0=sQuery(id+"F2.wireOp",EDGE,"E12");var subQ1=sQuery(id+"F2.wireOp",EDGE,"E9.5");var subQ2=makeQuery(id+"F2.imprint","INTERSECT",VERTEX,{"derivedFrom":[sQuery(id+"F2.wireOp",EDGE,"E8.0"),subQ1,subQ0]});Q49=makeQuery(id+"F2.imprint","IMPRINT",FACE,{"disambiguationData":[TD([[makeQuery(id+"F2.imprint","IMPRINT",EDGE,{"disambiguationData":[TD([[subQ2,-1.0]])],"derivedFrom":subQ1}),-1.0]])]});}
            var Q50;
            {var subQ0=sQuery(id+"F2.wireOp",EDGE,"E12");var subQ1=sQuery(id+"F2.wireOp",EDGE,"E9.6");var subQ2=makeQuery(id+"F2.imprint","INTERSECT",VERTEX,{"derivedFrom":[sQuery(id+"F2.wireOp",EDGE,"E8.1"),subQ1,subQ0]});Q50=makeQuery(id+"F2.imprint","IMPRINT",FACE,{"disambiguationData":[TD([[makeQuery(id+"F2.imprint","IMPRINT",EDGE,{"disambiguationData":[TD([[subQ2,-1.0]])],"derivedFrom":subQ1}),-1.0]])]});}
            var Q51;
            {var subQ0=sQuery(id+"F2.wireOp",EDGE,"E10");var subQ1=sQuery(id+"F2.wireOp",EDGE,"E9.6");var subQ2=makeQuery(id+"F2.imprint","INTERSECT",VERTEX,{"derivedFrom":[sQuery(id+"F2.wireOp",EDGE,"E8.2"),subQ1,subQ0]});Q51=makeQuery(id+"F2.imprint","IMPRINT",FACE,{"disambiguationData":[TD([[makeQuery(id+"F2.imprint","IMPRINT",EDGE,{"disambiguationData":[TD([[subQ2,1.0]])],"derivedFrom":subQ1}),-1.0]])]});}
            var Q52;
            {var subQ0=sQuery(id+"F2.wireOp",EDGE,"E10");var subQ1=sQuery(id+"F2.wireOp",EDGE,"E9.7");var subQ2=makeQuery(id+"F2.imprint","INTERSECT",VERTEX,{"derivedFrom":[sQuery(id+"F2.wireOp",EDGE,"E8.3"),subQ1,subQ0]});Q52=makeQuery(id+"F2.imprint","IMPRINT",FACE,{"disambiguationData":[TD([[makeQuery(id+"F2.imprint","IMPRINT",EDGE,{"disambiguationData":[TD([[subQ2,1.0]])],"derivedFrom":subQ1}),-1.0]])]});}
            var Q53;
            {var subQ0=sQuery(id+"F2.wireOp",EDGE,"E15");var subQ1=sQuery(id+"F2.wireOp",EDGE,"E9.8");var subQ2=makeQuery(id+"F2.imprint","INTERSECT",VERTEX,{"derivedFrom":[sQuery(id+"F2.wireOp",EDGE,"E8.3"),subQ1,subQ0]});Q53=makeQuery(id+"F2.imprint","IMPRINT",FACE,{"disambiguationData":[TD([[makeQuery(id+"F2.imprint","IMPRINT",EDGE,{"disambiguationData":[TD([[subQ2,-1.0]])],"derivedFrom":subQ1}),-1.0]])]});}
            var Q54;
            {var subQ0=sQuery(id+"F2.wireOp",EDGE,"E10");var subQ1=makeQuery(id+"F1.opRevolve","SWEPT_EDGE",EDGE,{"disambiguationData":[OSD([sQuery(id+"F0.wireOp",EDGE,"E1"),sQuery(id+"F0.wireOp",EDGE,"E5")])]});var subQ2=makeQuery(id+"F2.imprint","INTERSECT",VERTEX,{"disambiguationData":[OD(0.0)],"derivedFrom":[subQ1,subQ0]});Q54=makeQuery(id+"F2.imprint","IMPRINT",FACE,{"disambiguationData":[TD([[makeQuery(id+"F2.imprint","IMPRINT",EDGE,{"disambiguationData":[TD([[subQ2,-1.0]])],"derivedFrom":subQ0}),1.0]])]});}
            var Q55;
            {var subQ0=sQuery(id+"F2.wireOp",EDGE,"E11");var subQ1=makeQuery(id+"F1.opRevolve","SWEPT_EDGE",EDGE,{"disambiguationData":[OSD([sQuery(id+"F0.wireOp",EDGE,"E1"),sQuery(id+"F0.wireOp",EDGE,"E5")])]});var subQ2=makeQuery(id+"F2.imprint","INTERSECT",VERTEX,{"disambiguationData":[OD(0.0)],"derivedFrom":[subQ1,subQ0]});Q55=makeQuery(id+"F2.imprint","IMPRINT",FACE,{"disambiguationData":[TD([[makeQuery(id+"F2.imprint","IMPRINT",EDGE,{"disambiguationData":[TD([[subQ2,-1.0]])],"derivedFrom":subQ0}),1.0]])]});}
            var Q56;
            {var subQ0=sQuery(id+"F2.wireOp",EDGE,"E12");var subQ1=makeQuery(id+"F1.opRevolve","SWEPT_EDGE",EDGE,{"disambiguationData":[OSD([sQuery(id+"F0.wireOp",EDGE,"E1"),sQuery(id+"F0.wireOp",EDGE,"E5")])]});var subQ2=makeQuery(id+"F2.imprint","INTERSECT",VERTEX,{"disambiguationData":[OD(0.0)],"derivedFrom":[subQ1,subQ0]});Q56=makeQuery(id+"F2.imprint","IMPRINT",FACE,{"disambiguationData":[TD([[makeQuery(id+"F2.imprint","IMPRINT",EDGE,{"disambiguationData":[TD([[subQ2,-1.0]])],"derivedFrom":subQ0}),1.0]])]});}
            var Q57;
            {var subQ0=sQuery(id+"F2.wireOp",EDGE,"E13");var subQ1=makeQuery(id+"F1.opRevolve","SWEPT_EDGE",EDGE,{"disambiguationData":[OSD([sQuery(id+"F0.wireOp",EDGE,"E1"),sQuery(id+"F0.wireOp",EDGE,"E5")])]});var subQ2=makeQuery(id+"F2.imprint","INTERSECT",VERTEX,{"disambiguationData":[OD(0.0)],"derivedFrom":[subQ1,subQ0]});Q57=makeQuery(id+"F2.imprint","IMPRINT",FACE,{"disambiguationData":[TD([[makeQuery(id+"F2.imprint","IMPRINT",EDGE,{"disambiguationData":[TD([[subQ2,-1.0]])],"derivedFrom":subQ0}),1.0]])]});}
            var Q58;
            {var subQ0=sQuery(id+"F2.wireOp",EDGE,"E14");var subQ1=makeQuery(id+"F1.opRevolve","SWEPT_EDGE",EDGE,{"disambiguationData":[OSD([sQuery(id+"F0.wireOp",EDGE,"E1"),sQuery(id+"F0.wireOp",EDGE,"E5")])]});var subQ2=makeQuery(id+"F2.imprint","INTERSECT",VERTEX,{"disambiguationData":[OD(0.0)],"derivedFrom":[subQ1,subQ0]});Q58=makeQuery(id+"F2.imprint","IMPRINT",FACE,{"disambiguationData":[TD([[makeQuery(id+"F2.imprint","IMPRINT",EDGE,{"disambiguationData":[TD([[subQ2,-1.0]])],"derivedFrom":subQ0}),1.0]])]});}
            var Q59;
            {var subQ0=sQuery(id+"F2.wireOp",EDGE,"E15");var subQ1=makeQuery(id+"F1.opRevolve","SWEPT_EDGE",EDGE,{"disambiguationData":[OSD([sQuery(id+"F0.wireOp",EDGE,"E1"),sQuery(id+"F0.wireOp",EDGE,"E5")])]});var subQ2=makeQuery(id+"F2.imprint","INTERSECT",VERTEX,{"disambiguationData":[OD(0.0)],"derivedFrom":[subQ1,subQ0]});Q59=makeQuery(id+"F2.imprint","IMPRINT",FACE,{"disambiguationData":[TD([[makeQuery(id+"F2.imprint","IMPRINT",EDGE,{"disambiguationData":[TD([[subQ2,-1.0]])],"derivedFrom":subQ0}),1.0]])]});}
            extrude(context, id + "F5", {"entities" : qUnion([Q0, Q1, Q2, Q3, Q4, Q5, Q6, Q7, Q8, Q9, Q10, Q11, Q12, Q13, Q14, Q15, Q16, Q17, Q18, Q19, Q20, Q21, Q22, Q23, Q24, Q25, Q26, Q27, Q28, Q29, Q30, Q31, Q32, Q33, Q34, Q35, Q36, Q37, Q38, Q39, Q40, Q41, Q42, Q43, Q44, Q45, Q46, Q47, Q48, Q49, Q50, Q51, Q52, Q53, Q54, Q55, Q56, Q57, Q58, Q59]), "operationType" : NewBodyOperationType.REMOVE, "oppositeDirection" : true, "depth" : 25 * mm});
        }
        {
            var Q0;
            Q0=makeQuery(id+"F1.opRevolve","SWEPT_FACE",FACE,{"disambiguationData":[OSD([sQuery(id+"F0.wireOp",EDGE,"E2")])]});
            var sketch = newSketch(context, id + "F6", { "sketchPlane" : qUnion([Q0])});
            skCircle(sketch, "E18", {"center": v(0, 0) * mm, "radius": 2.5 * mm});
            skCircle(sketch, "E19", {"center": v(0, 0) * mm, "radius": 5.1 * mm});
            skSolve(sketch);
        }
        {
            var Q0;
            Q0 = qSketchRegion(id + "F6", true);
            extrude(context, id + "F7", {"entities" : qUnion([Q0]), "operationType" : NewBodyOperationType.ADD, "oppositeDirection" : true, "depth" : 25 * mm});
        }
        {
            var Q0;
            Q0=makeQuery(id+"F7.boolean.opBoolean","MERGE",FACE,{"derivedFrom":[makeQuery(id+"F1.opRevolve","SWEPT_FACE",FACE,{"disambiguationData":[OSD([sQuery(id+"F0.wireOp",EDGE,"E2")])]}),makeQuery(id+"F7.opExtrude","CAP_FACE",FACE,{"disambiguationData":[OSD([sQuery(id+"F6.wireOp",EDGE,"E18"),sQuery(id+"F6.wireOp",EDGE,"E19")])],"isStart":true})]});
            var sketch = newSketch(context, id + "F8", { "sketchPlane" : qUnion([Q0])});
            skCircle(sketch, "E20", {"center": v(0, 0) * mm, "radius": 3 * mm});
            skSolve(sketch);
        }
        {
            var Q0;
            Q0 = qSketchRegion(id + "F8", true);
            extrude(context, id + "F9", {"entities" : qUnion([Q0]), "operationType" : NewBodyOperationType.REMOVE, "oppositeDirection" : true, "depth" : 20 * mm});
        }
    });
